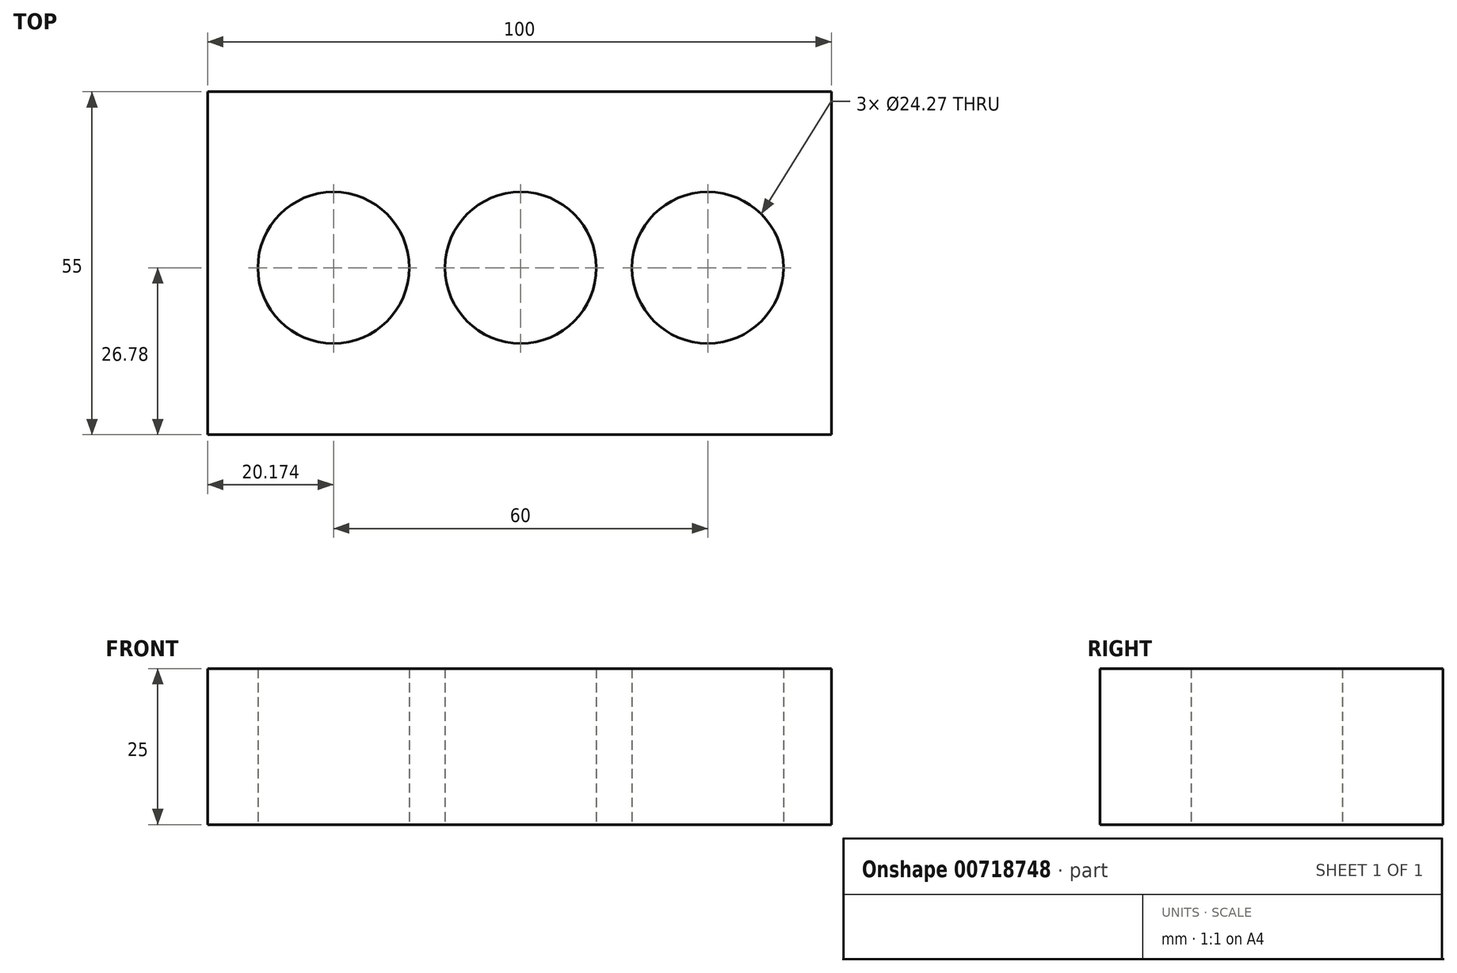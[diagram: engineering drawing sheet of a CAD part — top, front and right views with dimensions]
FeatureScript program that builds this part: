
annotation { "Feature Type Name" : "Feature", "Feature Type Description" : "" }
export const myFeature = defineFeature(function(context is Context, id is Id, definition is map)
    precondition{}
    {
        {
            var Q0;
            Q0=qCreatedBy(makeId("Top.planeOp"),FACE);
            var sketch = newSketch(context, id + "F0", { "sketchPlane" : qUnion([Q0])});
            skLineSegment(sketch, "E0.bottom", {"start": v(0, 0) * mm, "end": v(100, 0) * mm});
            skLineSegment(sketch, "E0.top", {"start": v(0, 55) * mm, "end": v(100, 55) * mm});
            skLineSegment(sketch, "E0.left", {"start": v(0, 0) * mm, "end": v(0, 55) * mm});
            skLineSegment(sketch, "E0.right", {"start": v(100, 0) * mm, "end": v(100, 55) * mm});
            skSolve(sketch);
        }
        {
            var Q0;
            Q0 = qSketchRegion(id + "F0", true);
            extrude(context, id + "F1", {"entities" : qUnion([Q0]), "depth" : 25 * mm, "offsetDistance" : 25 * mm});
        }
        {
            var Q0;
            Q0=qCreatedBy(makeId("Top.planeOp"),FACE);
            var sketch = newSketch(context, id + "F2", { "sketchPlane" : qUnion([Q0])});
            skCircle(sketch, "E1", {"center": v(20.17, 26.78) * mm, "radius": 12.14 * mm});
            skCircle(sketch, "E2.1.0.0", {"center": v(50.17, 26.78) * mm, "radius": 12.14 * mm});
            skCircle(sketch, "E2.2.0.0", {"center": v(80.17, 26.78) * mm, "radius": 12.14 * mm});
            skLineSegment(sketch, "E2.direction1", {"start": v(20.17, 26.78) * mm, "end": v(50.17, 26.78) * mm, "construction": true});
            skSolve(sketch);
        }
        {
            var Q0;
            Q0=makeQuery(id+"F2.imprint","IMPRINT",FACE,{"disambiguationData":[TD([[makeQuery(id+"F2.imprint","IMPRINT",EDGE,{"derivedFrom":sQuery(id+"F2.wireOp",EDGE,"E2.2.0.0")}),1.0]])]});
            var Q1;
            Q1=makeQuery(id+"F2.imprint","IMPRINT",FACE,{"disambiguationData":[TD([[makeQuery(id+"F2.imprint","IMPRINT",EDGE,{"derivedFrom":sQuery(id+"F2.wireOp",EDGE,"E2.1.0.0")}),1.0]])]});
            var Q2;
            Q2=makeQuery(id+"F2.imprint","IMPRINT",FACE,{"disambiguationData":[TD([[makeQuery(id+"F2.imprint","IMPRINT",EDGE,{"derivedFrom":sQuery(id+"F2.wireOp",EDGE,"E1")}),1.0]])]});
            extrude(context, id + "F3", {"entities" : qUnion([Q0, Q1, Q2]), "operationType" : NewBodyOperationType.REMOVE, "depth" : 25 * mm, "offsetDistance" : 25 * mm});
        }
    });
